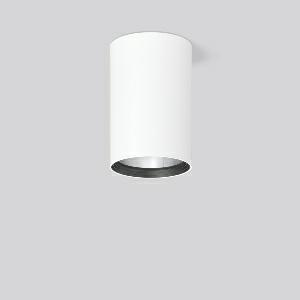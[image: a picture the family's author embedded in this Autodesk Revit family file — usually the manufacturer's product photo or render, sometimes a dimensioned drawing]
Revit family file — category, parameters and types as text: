
# Revit family: heledon_maxi_a_931216_002_3_76_becd
name_source: partatom
category: Lighting Fixtures
units: mm (PartAtom-declared; Revit-internal decimal feet)

## family parameters
Cut with Voids When Loaded = No
Host = Face
Light Source = No
Part Type = Normal
Room Calculation Point = No
Round Connector Dimension = Use Diameter
Shared = No

## types (1)
- HELEDON maxi A (1 x LED Modul 935, 3300 lm, 3500)
    Apparent Load = 25 VA
    Approval mark = CE
    CIE Flux Codes = 100 100 100 100 100
    Color Rendering = 92
    Color Temperature = 3500
    Default Elevation = 1800 mm
    Description = Series: HELEDON maxi
Cylindrical surface-mounted downlight. Housing: die-cast aluminium, powder-coated. Internal ceiling frame polycarbonate with bayonet mounting. Black plastic ring and recessed LED to prevent glare from the side. Optical assembly with reflector made of MIRO-Silver with 98% total light reflection for outstanding efficiency - can be changed without tools. Best colour rendering index Ra>90. Suitable for Ceiling mounting. Easy installation with a separate ceiling frame with bayonet mounting and plug connection. Driver integrated. Connected via plug-in connector. High quality converter without flickering and stroboscopic effect. The following accessories can be mounted without use of tools: interchangeable lenses, decorative glasses, honeycomb louvre, clear and frosted diffusers, white interchangeable plastic ring. 
Colour: traffic white, matt (RAL 9016)
Diameter: 123 mm
Height: 183 mm
Lamp: LED
Socket: without socket
Colour temperature: 3500K
Colour rendering index (CRI): 92
System power: 25 W
Rated luminous flux: 3300 lm
Luminous efficiency: 132 lm/W
Control gear: Converter, dimmable, DALI
Protection class: I
Type of protection: IP 20
    Height = 183 mm
    Lamp = 1 x LED Modul 935
    Lamp Light Flux = 3300 lm
    Lamp count = 1
    Length = 123 mm
    Lifetime = 50000 h
    Luminous efficacy = 132 lm/W
    Manufacturer = RZB
    ModVariant = No
    Model = 931216.002.3.76
    Mounting Place = Ceiling
    Mounting Type = Surface mounted
    Number of Poles = 1
    OnlyDefault = Yes
    Power Factor = 1
    Product Name = HELEDON maxi A
    Product group = Surface mounted downlights
    ProductGroupID = 302
    Protection Class = Protection class I
    Protection Degree = IP 20
    RLX_Detail_Level = 1
    RLX_Emergency_Light_Flux = 0 lm
    RLX_Emergency_Type = 0
    RLX_Emergency_Type_DB = No
    RlxData = <blob elided: 98113 chars, md5=3b33dd10>
    Socket = socket
    Standby Power = 0 W
    System Light Flux = 3300 lm
    System Power = 25 W
    Type Comments = Product without accessories
    Type Image = 931192.002.jpg
    URL = http://relux.com
    VarID = ---
    Voltage = 230 V
    Voltage Range = 220-240 V
    Weight = 0.00 kg
    Width = 0 mm  [stored 0 ft]

note: [stored X ft] marks values corroborated as IEEE doubles in the binary element streams (Revit-internal decimal feet)

## geometry (parser evidence)
native form markers: Blend x4, Sweep x11
no freeform markers — native parametric forms only
